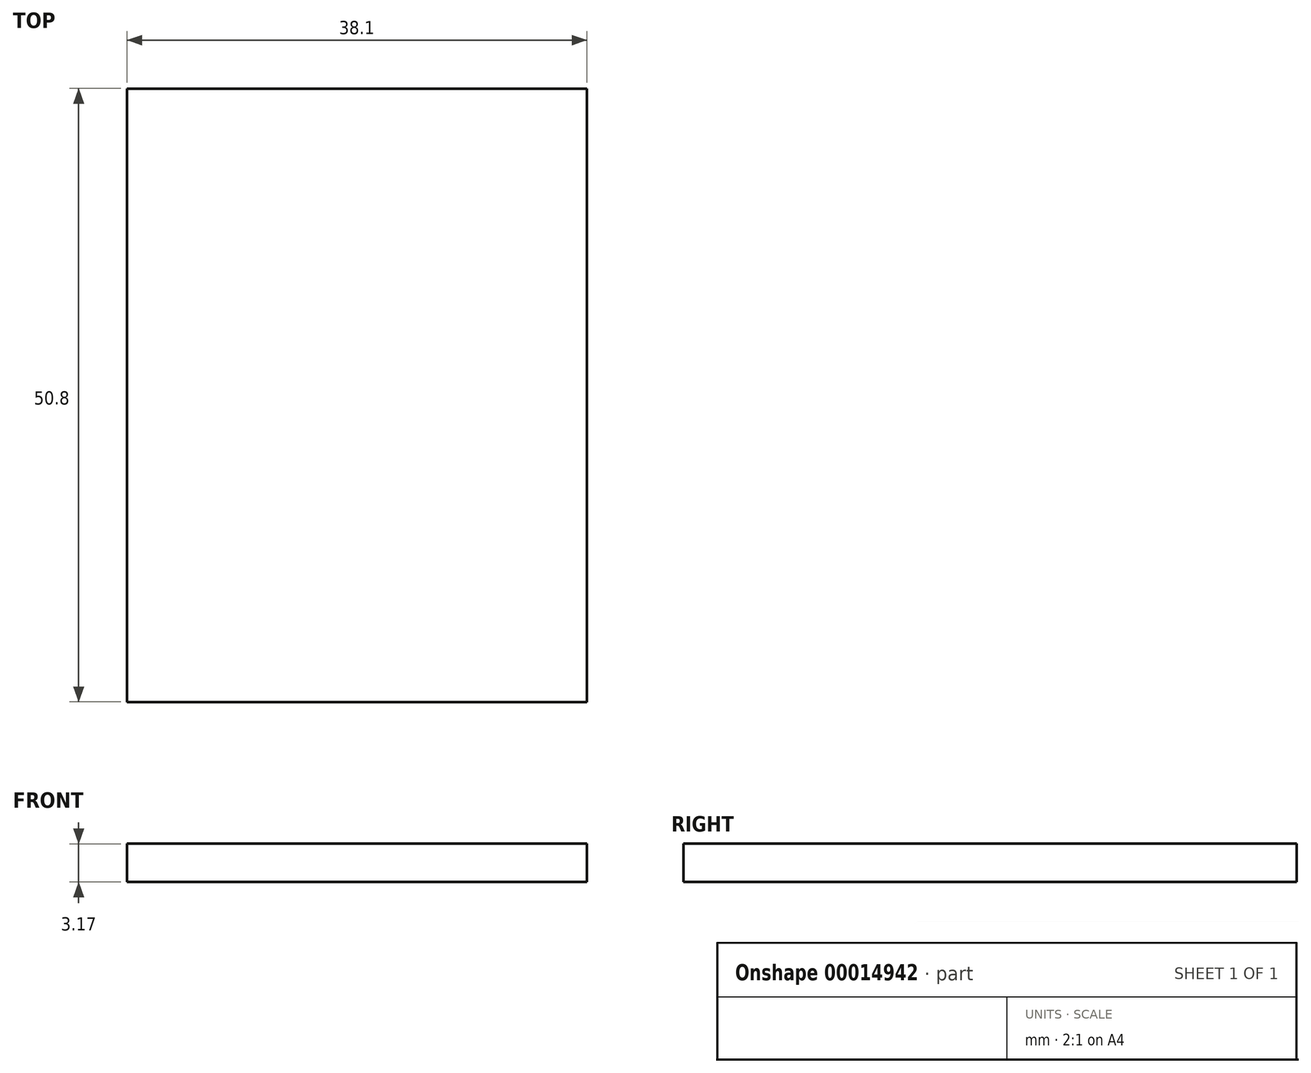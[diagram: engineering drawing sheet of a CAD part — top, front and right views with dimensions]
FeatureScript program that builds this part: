
annotation { "Feature Type Name" : "Feature", "Feature Type Description" : "" }
export const myFeature = defineFeature(function(context is Context, id is Id, definition is map)
    precondition{}
    {
        {
            var Q0;
            Q0=qCreatedBy(makeId("Top.planeOp"),FACE);
            var sketch = newSketch(context, id + "F0", { "sketchPlane" : qUnion([Q0])});
            skLineSegment(sketch, "E0.bottom", {"start": v(-34.92, 39.4) * mm, "end": v(3.18, 39.4) * mm});
            skLineSegment(sketch, "E0.top", {"start": v(-34.92, -11.4) * mm, "end": v(3.18, -11.4) * mm});
            skLineSegment(sketch, "E0.left", {"start": v(-34.92, 39.4) * mm, "end": v(-34.92, -11.4) * mm});
            skLineSegment(sketch, "E0.right", {"start": v(3.18, 39.4) * mm, "end": v(3.18, -11.4) * mm});
            skSolve(sketch);
        }
        {
            var Q0;
            Q0=makeQuery(id+"F0.imprint","IMPRINT",FACE,{"disambiguationData":[TD([[makeQuery(id+"F0.imprint","IMPRINT",EDGE,{"derivedFrom":sQuery(id+"F0.wireOp",EDGE,"E0.bottom")}),-1.0]])]});
            extrude(context, id + "F1", {"entities" : qUnion([Q0]), "depth" : 3.17 * mm});
        }
    });
